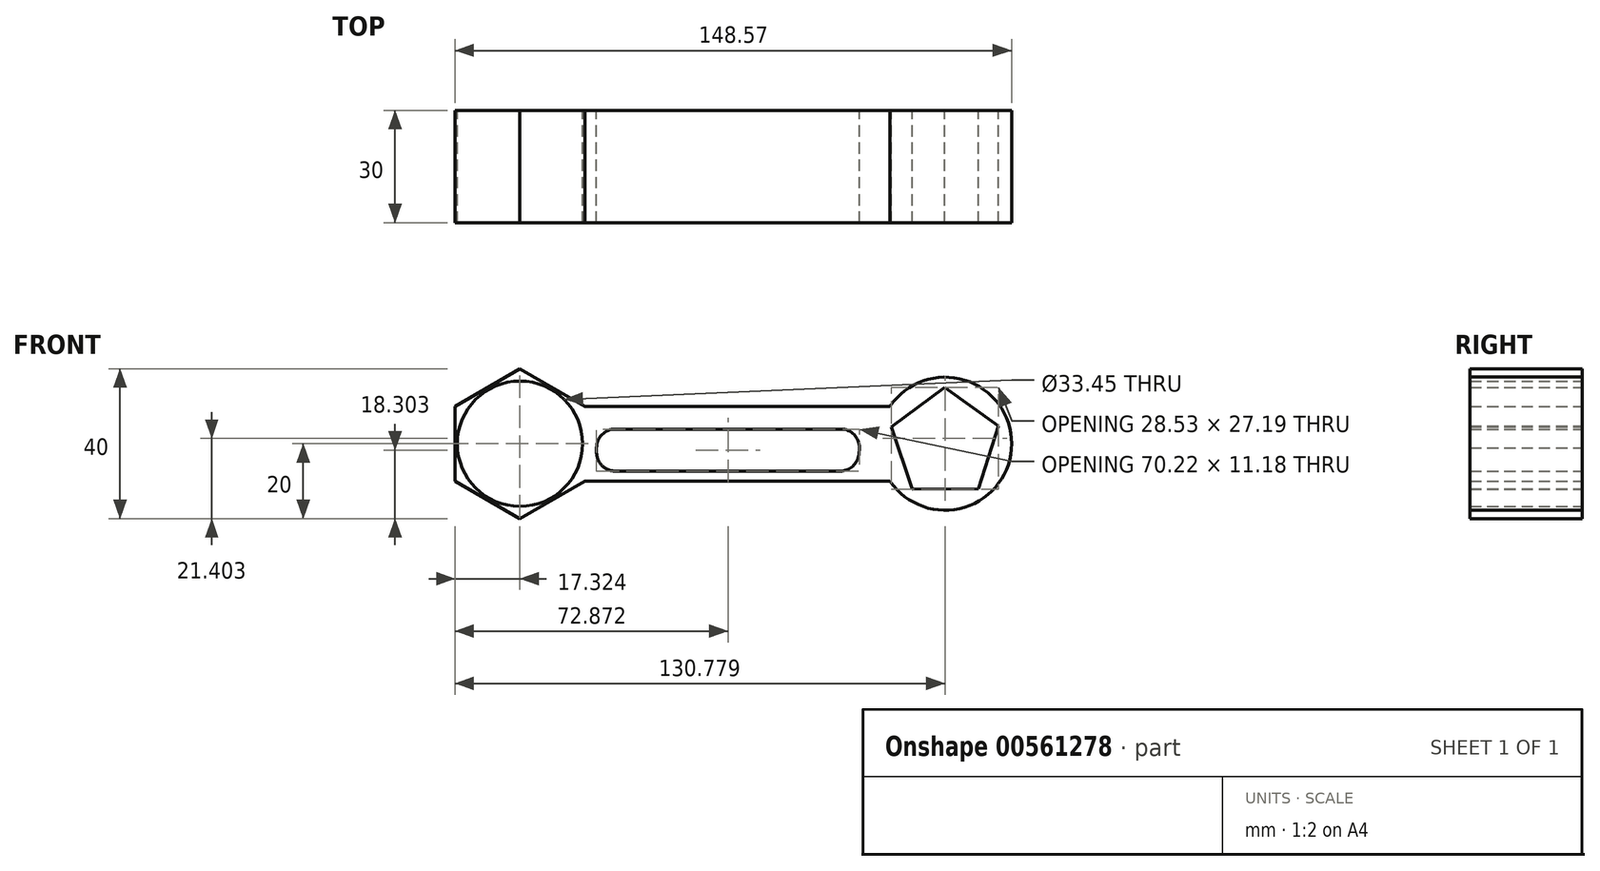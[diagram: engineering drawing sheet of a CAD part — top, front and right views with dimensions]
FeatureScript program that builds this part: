
annotation { "Feature Type Name" : "Feature", "Feature Type Description" : "" }
export const myFeature = defineFeature(function(context is Context, id is Id, definition is map)
    precondition{}
    {
        {
            var Q0;
            Q0=qCreatedBy(makeId("Front.planeOp"),FACE);
            var sketch = newSketch(context, id + "F0", { "sketchPlane" : qUnion([Q0])});
            skCircle(sketch, "E0.cCircle", {"center": v(0, 0) * mm, "radius": 12.14 * mm, "construction": true});
            skLineSegment(sketch, "E0.0", {"start": v(8.9, -12.08) * mm, "end": v(14.23, 4.73) * mm});
            skLineSegment(sketch, "E0.1", {"start": v(-8.74, -12.2) * mm, "end": v(8.9, -12.08) * mm});
            skLineSegment(sketch, "E0.2", {"start": v(-14.3, 4.54) * mm, "end": v(-8.74, -12.2) * mm});
            skLineSegment(sketch, "E0.3", {"start": v(-0.1, 15) * mm, "end": v(-14.3, 4.54) * mm});
            skLineSegment(sketch, "E0.4", {"start": v(14.23, 4.73) * mm, "end": v(-0.1, 15) * mm});
            skPoint(sketch, "E0.0.midPoint", {"position": v(11.57, -3.67) * mm});
            skCircle(sketch, "E1.cCircle", {"center": v(-113.49, 0) * mm, "radius": 17.32 * mm, "construction": true});
            skLineSegment(sketch, "E1.0", {"start": v(-96.17, -10) * mm, "end": v(-113.49, -20) * mm});
            skLineSegment(sketch, "E1.1", {"start": v(-113.49, -20) * mm, "end": v(-130.8, -10) * mm});
            skLineSegment(sketch, "E1.2", {"start": v(-130.8, -10) * mm, "end": v(-130.8, 10) * mm});
            skLineSegment(sketch, "E1.3", {"start": v(-130.8, 10) * mm, "end": v(-113.49, 20) * mm});
            skLineSegment(sketch, "E1.4", {"start": v(-113.49, 20) * mm, "end": v(-96.17, 10) * mm});
            skLineSegment(sketch, "E1.5", {"start": v(-96.17, 10) * mm, "end": v(-96.17, -10) * mm});
            skPoint(sketch, "E1.0.midPoint", {"position": v(-104.83, -15) * mm});
            skCircle(sketch, "E2", {"center": v(-113.49, 0) * mm, "radius": 16.72 * mm});
            skCircle(sketch, "E3", {"center": v(0, 0) * mm, "radius": 17.76 * mm});
            skLineSegment(sketch, "E4", {"start": v(-100.08, 10) * mm, "end": v(-14.68, 10) * mm});
            skLineSegment(sketch, "E5", {"start": v(-100.08, -10) * mm, "end": v(-14.68, -10) * mm});
            skLineSegment(sketch, "E6", {"start": v(-88.05, 3.9) * mm, "end": v(-27.83, 3.9) * mm});
            skLineSegment(sketch, "E7", {"start": v(-28.01, -7.29) * mm, "end": v(-88.05, -7.29) * mm});
            skLineSegment(sketch, "E8", {"start": v(-93.05, -2.29) * mm, "end": v(-93.05, -1.1) * mm});
            skArc(sketch, "E9.filletArc", {"start": v(-88.05, 3.9) * mm, "mid": v(-91.58, 2.43) * mm, "end": v(-93.05, -1.1) * mm});
            skArc(sketch, "E10.filletArc", {"start": v(-22.83, -1.1) * mm, "mid": v(-24.3, 2.43) * mm, "end": v(-27.83, 3.9) * mm});
            skArc(sketch, "E11.filletArc", {"start": v(-93.05, -2.29) * mm, "mid": v(-91.58, -5.82) * mm, "end": v(-88.05, -7.29) * mm});
            skLineSegment(sketch, "E12", {"start": v(-23.05, -2.9) * mm, "end": v(-22.83, -1.1) * mm});
            skArc(sketch, "E13.filletArc", {"start": v(-28.01, -7.29) * mm, "mid": v(-24.7, -6.03) * mm, "end": v(-23.05, -2.9) * mm});
            skSolve(sketch);
        }
        {
            var Q0;
            Q0 = qSketchRegion(id + "F0", true);
            extrude(context, id + "F1", {"entities" : qUnion([Q0]), "depth" : 30 * mm, "offsetDistance" : 25 * mm});
        }
    });
